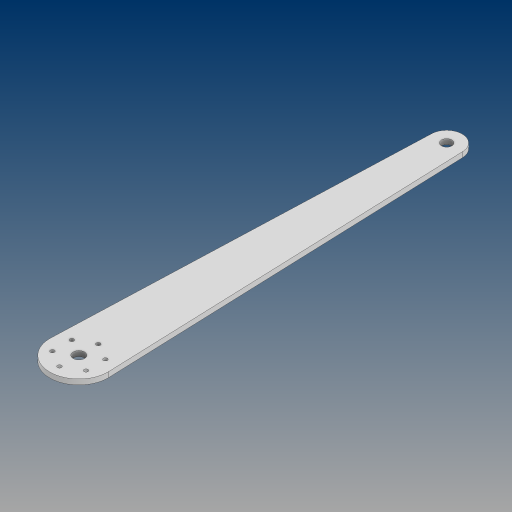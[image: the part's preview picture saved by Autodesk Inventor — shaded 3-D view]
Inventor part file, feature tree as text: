
AUTODESK INVENTOR PART (.ipt)
format: ipt  version: 2024.3 (Build 283343000, 343)  size: 112,640 bytes
history: native  units: in
note: dims shown in document units (in); Inventor stores cm internally (conversion verified against a paired STEP export)
features: extrude x1, sketch x1
ambient origin geometry x8: Origin, YZ Plane, XZ Plane, XY Plane, X Axis, Y Axis, Z Axis, Center Point
bodies: Solid1 (feature_tree)
feature tree (2):
  extrude  "Extrusion1"  Depth=0.25in
  sketch  "Sketch1"  dims[d0=17.8in d1=0.5in d2=0.55in d3=2.31in d4=0.25in d5=0.5in d6=1.875in d7=0.19in d8=2.3622in d10=360.0deg d12=0.25in d13=0.0in]
